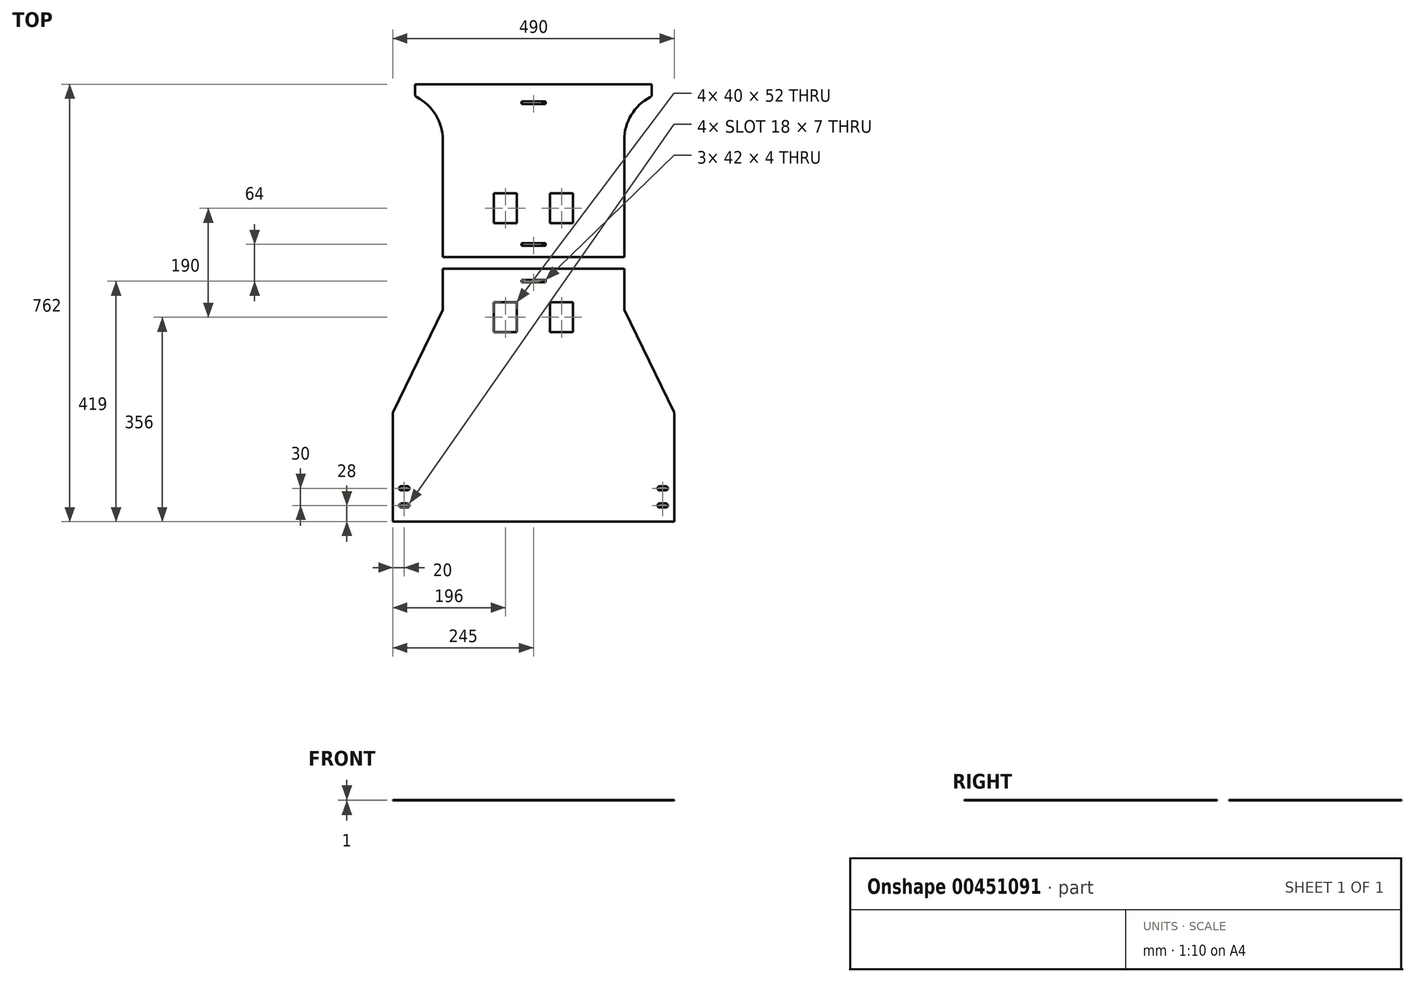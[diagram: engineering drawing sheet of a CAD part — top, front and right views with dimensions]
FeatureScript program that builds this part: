
annotation { "Feature Type Name" : "Feature", "Feature Type Description" : "" }
export const myFeature = defineFeature(function(context is Context, id is Id, definition is map)
    precondition{}
    {
        {
            var Q0;
            Q0=qCreatedBy(makeId("Top.planeOp"),FACE);
            var sketch = newSketch(context, id + "F0", { "sketchPlane" : qUnion([Q0])});
            skLineSegment(sketch, "E0.bottom", {"start": v(0, 0) * mm, "end": v(490, 0) * mm});
            skLineSegment(sketch, "E0.top", {"start": v(0, 190) * mm, "end": v(490, 190) * mm});
            skLineSegment(sketch, "E0.left", {"start": v(0, 0) * mm, "end": v(0, 190) * mm});
            skLineSegment(sketch, "E0.right", {"start": v(490, 0) * mm, "end": v(490, 190) * mm});
            skLineSegment(sketch, "E1", {"start": v(0, 190) * mm, "end": v(87, 369) * mm});
            skLineSegment(sketch, "E2", {"start": v(87, 369) * mm, "end": v(87, 441) * mm});
            skLineSegment(sketch, "E3", {"start": v(87, 441) * mm, "end": v(403, 441) * mm});
            skLineSegment(sketch, "E4", {"start": v(403, 441) * mm, "end": v(403, 369) * mm});
            skLineSegment(sketch, "E5", {"start": v(403, 369) * mm, "end": v(490, 190) * mm});
            skPoint(sketch, "E6", {"position": v(245, 441) * mm});
            skPoint(sketch, "E7", {"position": v(245, 0) * mm});
            skLineSegment(sketch, "E8.bottom", {"start": v(14.5, 24.5) * mm, "end": v(14.5, 31.5) * mm, "construction": true});
            skLineSegment(sketch, "E8.top", {"start": v(25.5, 24.5) * mm, "end": v(25.5, 31.5) * mm, "construction": true});
            skLineSegment(sketch, "E8.left", {"start": v(14.5, 24.5) * mm, "end": v(25.5, 24.5) * mm});
            skLineSegment(sketch, "E8.right", {"start": v(14.5, 31.5) * mm, "end": v(25.5, 31.5) * mm});
            skPoint(sketch, "E8.middle", {"position": v(20, 28) * mm});
            skArc(sketch, "E9", {"start": v(25.5, 24.5) * mm, "mid": v(29, 28) * mm, "end": v(25.5, 31.5) * mm});
            skArc(sketch, "E10", {"start": v(14.5, 31.5) * mm, "mid": v(11, 28) * mm, "end": v(14.5, 24.5) * mm});
            skLineSegment(sketch, "E11.bottom", {"start": v(14.5, 54.5) * mm, "end": v(14.5, 61.5) * mm, "construction": true});
            skLineSegment(sketch, "E11.top", {"start": v(25.5, 54.5) * mm, "end": v(25.5, 61.5) * mm, "construction": true});
            skLineSegment(sketch, "E11.left", {"start": v(14.5, 54.5) * mm, "end": v(25.5, 54.5) * mm});
            skLineSegment(sketch, "E11.right", {"start": v(14.5, 61.5) * mm, "end": v(25.5, 61.5) * mm});
            skPoint(sketch, "E11.middle", {"position": v(20, 58) * mm});
            skArc(sketch, "E12", {"start": v(25.5, 54.5) * mm, "mid": v(29, 58) * mm, "end": v(25.5, 61.5) * mm});
            skArc(sketch, "E13", {"start": v(14.5, 61.5) * mm, "mid": v(11, 58) * mm, "end": v(14.5, 54.5) * mm});
            skLineSegment(sketch, "E14", {"start": v(245, 42.53) * mm, "end": v(245, 125.1) * mm, "construction": true});
            skLineSegment(sketch, "E15.MirrorCS", {"start": v(475.5, 24.5) * mm, "end": v(475.5, 31.5) * mm, "construction": true});
            skArc(sketch, "E16.MirrorCS", {"start": v(464.5, 54.5) * mm, "mid": v(461, 58) * mm, "end": v(464.5, 61.5) * mm});
            skArc(sketch, "E17.MirrorCS", {"start": v(464.5, 24.5) * mm, "mid": v(461, 28) * mm, "end": v(464.5, 31.5) * mm});
            skLineSegment(sketch, "E18.MirrorCS", {"start": v(464.5, 54.5) * mm, "end": v(464.5, 61.5) * mm, "construction": true});
            skArc(sketch, "E19.MirrorCS", {"start": v(475.5, 31.5) * mm, "mid": v(479, 28) * mm, "end": v(475.5, 24.5) * mm});
            skLineSegment(sketch, "E20.MirrorCS", {"start": v(464.5, 24.5) * mm, "end": v(464.5, 31.5) * mm, "construction": true});
            skLineSegment(sketch, "E21.MirrorCS", {"start": v(475.5, 54.5) * mm, "end": v(475.5, 61.5) * mm, "construction": true});
            skArc(sketch, "E22.MirrorCS", {"start": v(475.5, 61.5) * mm, "mid": v(479, 58) * mm, "end": v(475.5, 54.5) * mm});
            skLineSegment(sketch, "E23.MirrorCS", {"start": v(475.5, 31.5) * mm, "end": v(464.5, 31.5) * mm});
            skLineSegment(sketch, "E24.MirrorCS", {"start": v(475.5, 24.5) * mm, "end": v(464.5, 24.5) * mm});
            skLineSegment(sketch, "E25.MirrorCS", {"start": v(475.5, 61.5) * mm, "end": v(464.5, 61.5) * mm});
            skLineSegment(sketch, "E26.MirrorCS", {"start": v(475.5, 54.5) * mm, "end": v(464.5, 54.5) * mm});
            skPoint(sketch, "E27.MirrorP", {"position": v(470, 58) * mm});
            skPoint(sketch, "E28.MirrorP", {"position": v(470, 28) * mm});
            skLineSegment(sketch, "E29", {"start": v(87, 461) * mm, "end": v(403, 461) * mm});
            skLineSegment(sketch, "E30", {"start": v(87, 461) * mm, "end": v(87, 665) * mm});
            skLineSegment(sketch, "E31", {"start": v(87, 665) * mm, "end": v(39, 741) * mm, "construction": true});
            skLineSegment(sketch, "E32", {"start": v(39, 741) * mm, "end": v(39, 762) * mm});
            skLineSegment(sketch, "E33", {"start": v(39, 762) * mm, "end": v(451, 762) * mm});
            skLineSegment(sketch, "E34", {"start": v(451, 762) * mm, "end": v(451, 741) * mm});
            skLineSegment(sketch, "E35", {"start": v(451, 741) * mm, "end": v(403, 665) * mm, "construction": true});
            skLineSegment(sketch, "E36", {"start": v(403, 665) * mm, "end": v(403, 461) * mm});
            skPoint(sketch, "E37", {"position": v(245, 762) * mm});
            skPoint(sketch, "E38", {"position": v(245, 461) * mm});
            skArc(sketch, "E39", {"start": v(87, 665) * mm, "mid": v(74, 709.94) * mm, "end": v(39, 741) * mm});
            skArc(sketch, "E40.MirrorCS", {"start": v(403, 665) * mm, "mid": v(416, 709.94) * mm, "end": v(451, 741) * mm});
            skSolve(sketch);
        }
        {
            var Q0;
            Q0 = qSketchRegion(id + "F0", true);
            extrude(context, id + "F1", {"entities" : qUnion([Q0]), "depth" : 1 * mm, "offsetDistance" : 25 * mm});
        }
        {
            var Q0;
            Q0=makeQuery(id+"F1.opExtrude","SWEPT_EDGE",EDGE,{"disambiguationData":[OSD([sQuery(id+"F0.wireOp",EDGE,"E32"),sQuery(id+"F0.wireOp",EDGE,"E39")])]});
            var Q1;
            Q1=makeQuery(id+"F1.opExtrude","SWEPT_EDGE",EDGE,{"disambiguationData":[OSD([sQuery(id+"F0.wireOp",EDGE,"E34"),sQuery(id+"F0.wireOp",EDGE,"E40.MirrorCS")])]});
            var Q2;
            Q2=makeQuery(id+"F1.opExtrude","SWEPT_EDGE",EDGE,{"disambiguationData":[OSD([sQuery(id+"F0.wireOp",EDGE,"E0.top"),sQuery(id+"F0.wireOp",EDGE,"E0.left"),sQuery(id+"F0.wireOp",EDGE,"E1")])]});
            var Q3;
            Q3=makeQuery(id+"F1.opExtrude","SWEPT_EDGE",EDGE,{"disambiguationData":[OSD([sQuery(id+"F0.wireOp",EDGE,"E0.top"),sQuery(id+"F0.wireOp",EDGE,"E0.right"),sQuery(id+"F0.wireOp",EDGE,"E5")])]});
            fillet(context, id + "F2", {"entities" : qUnion([Q0, Q1, Q2, Q3]), "tangentPropagation" : true, "radius" : 5 * mm, "defaultsChanged" : false, "vertexSettings" : [], "allowEdgeOverflow" : false});
        }
        {
            var Q0;
            Q0=makeQuery(id+"F1.opExtrude","CAP_FACE",FACE,{"disambiguationData":[OSD([sQuery(id+"F0.wireOp",EDGE,"E0.bottom"),sQuery(id+"F0.wireOp",EDGE,"E0.left"),sQuery(id+"F0.wireOp",EDGE,"E0.right"),sQuery(id+"F0.wireOp",EDGE,"E1"),sQuery(id+"F0.wireOp",EDGE,"E2"),sQuery(id+"F0.wireOp",EDGE,"E3"),sQuery(id+"F0.wireOp",EDGE,"E4"),sQuery(id+"F0.wireOp",EDGE,"E5"),sQuery(id+"F0.wireOp",EDGE,"E8.left"),sQuery(id+"F0.wireOp",EDGE,"E8.right"),sQuery(id+"F0.wireOp",EDGE,"E9"),sQuery(id+"F0.wireOp",EDGE,"E10"),sQuery(id+"F0.wireOp",EDGE,"E11.left"),sQuery(id+"F0.wireOp",EDGE,"E11.right"),sQuery(id+"F0.wireOp",EDGE,"E12"),sQuery(id+"F0.wireOp",EDGE,"E13"),sQuery(id+"F0.wireOp",EDGE,"E16.MirrorCS"),sQuery(id+"F0.wireOp",EDGE,"E17.MirrorCS"),sQuery(id+"F0.wireOp",EDGE,"E19.MirrorCS"),sQuery(id+"F0.wireOp",EDGE,"E22.MirrorCS"),sQuery(id+"F0.wireOp",EDGE,"E23.MirrorCS"),sQuery(id+"F0.wireOp",EDGE,"E24.MirrorCS"),sQuery(id+"F0.wireOp",EDGE,"E25.MirrorCS"),sQuery(id+"F0.wireOp",EDGE,"E26.MirrorCS")])],"isStart":false});
            var sketch = newSketch(context, id + "F3", { "sketchPlane" : qUnion([Q0])});
            skPoint(sketch, "E41.middle.positionSnap0", {"position": v(245, 0) * mm});
            skPoint(sketch, "E41.centerSnap0", {"position": v(245, 0) * mm});
            skLineSegment(sketch, "E42.bottom", {"start": v(211, 330) * mm, "end": v(216, 330) * mm});
            skLineSegment(sketch, "E42.top", {"start": v(211, 377) * mm, "end": v(216, 377) * mm});
            skLineSegment(sketch, "E42.left", {"start": v(211, 330) * mm, "end": v(211, 377) * mm, "construction": true});
            skLineSegment(sketch, "E42.right", {"start": v(216, 330) * mm, "end": v(216, 377) * mm});
            skLineSegment(sketch, "E43.bottom", {"start": v(216, 377) * mm, "end": v(176, 377) * mm, "construction": true});
            skLineSegment(sketch, "E43.top", {"start": v(216, 382) * mm, "end": v(176, 382) * mm});
            skLineSegment(sketch, "E43.left", {"start": v(216, 377) * mm, "end": v(216, 382) * mm});
            skLineSegment(sketch, "E43.right", {"start": v(176, 377) * mm, "end": v(176, 382) * mm});
            skLineSegment(sketch, "E44", {"start": v(245, 0) * mm, "end": v(245, -104.71) * mm, "construction": true});
            skLineSegment(sketch, "E45.bottom", {"start": v(266, 417) * mm, "end": v(224, 417) * mm});
            skLineSegment(sketch, "E45.top", {"start": v(266, 421) * mm, "end": v(224, 421) * mm});
            skLineSegment(sketch, "E45.left", {"start": v(266, 417) * mm, "end": v(266, 421) * mm});
            skLineSegment(sketch, "E45.right", {"start": v(224, 417) * mm, "end": v(224, 421) * mm});
            skPoint(sketch, "E45.middle", {"position": v(245, 419) * mm});
            skPoint(sketch, "E45.middle.positionSnap0", {"position": v(245, 441) * mm});
            skPoint(sketch, "E45.centerSnap0", {"position": v(245, 441) * mm});
            skLineSegment(sketch, "E46", {"start": v(176, 377) * mm, "end": v(176, 330) * mm});
            skLineSegment(sketch, "E47", {"start": v(176, 330) * mm, "end": v(211, 330) * mm});
            skLineSegment(sketch, "E48.MirrorCS", {"start": v(279, 377) * mm, "end": v(274, 377) * mm});
            skLineSegment(sketch, "E49.MirrorCS", {"start": v(314, 330) * mm, "end": v(279, 330) * mm});
            skLineSegment(sketch, "E50.MirrorCS", {"start": v(279, 330) * mm, "end": v(279, 377) * mm, "construction": true});
            skLineSegment(sketch, "E51.MirrorCS", {"start": v(274, 377) * mm, "end": v(314, 377) * mm, "construction": true});
            skLineSegment(sketch, "E52.MirrorCS", {"start": v(274, 330) * mm, "end": v(274, 377) * mm});
            skLineSegment(sketch, "E53.MirrorCS", {"start": v(279, 330) * mm, "end": v(274, 330) * mm});
            skLineSegment(sketch, "E54.MirrorCS", {"start": v(314, 377) * mm, "end": v(314, 330) * mm});
            skLineSegment(sketch, "E55.MirrorCS", {"start": v(274, 377) * mm, "end": v(274, 382) * mm});
            skLineSegment(sketch, "E56.MirrorCS", {"start": v(274, 382) * mm, "end": v(314, 382) * mm});
            skLineSegment(sketch, "E57.MirrorCS", {"start": v(314, 377) * mm, "end": v(314, 382) * mm});
            skSolve(sketch);
        }
        {
            var Q0;
            Q0 = qSketchRegion(id + "F3", true);
            extrude(context, id + "F4", {"entities" : qUnion([Q0]), "operationType" : NewBodyOperationType.REMOVE, "oppositeDirection" : true, "depth" : 25 * mm, "offsetDistance" : 25 * mm});
        }
        {
            var Q0;
            Q0=makeQuery(id+"F1.opExtrude","CAP_FACE",FACE,{"disambiguationData":[OSD([sQuery(id+"F0.wireOp",EDGE,"E29"),sQuery(id+"F0.wireOp",EDGE,"E30"),sQuery(id+"F0.wireOp",EDGE,"E32"),sQuery(id+"F0.wireOp",EDGE,"E33"),sQuery(id+"F0.wireOp",EDGE,"E34"),sQuery(id+"F0.wireOp",EDGE,"E36"),sQuery(id+"F0.wireOp",EDGE,"E39"),sQuery(id+"F0.wireOp",EDGE,"E40.MirrorCS")])],"isStart":false});
            var sketch = newSketch(context, id + "F5", { "sketchPlane" : qUnion([Q0])});
            skLineSegment(sketch, "E58.bottom", {"start": v(266, 481) * mm, "end": v(224, 481) * mm});
            skLineSegment(sketch, "E58.top", {"start": v(266, 485) * mm, "end": v(224, 485) * mm});
            skLineSegment(sketch, "E58.left", {"start": v(266, 481) * mm, "end": v(266, 485) * mm});
            skLineSegment(sketch, "E58.right", {"start": v(224, 481) * mm, "end": v(224, 485) * mm});
            skPoint(sketch, "E58.middle", {"position": v(245, 483) * mm});
            skPoint(sketch, "E58.middle.positionSnap0", {"position": v(245, 762) * mm});
            skPoint(sketch, "E58.centerSnap0", {"position": v(245, 762) * mm});
            skLineSegment(sketch, "E59.bottom", {"start": v(211, 572) * mm, "end": v(216, 572) * mm});
            skLineSegment(sketch, "E59.top", {"start": v(211, 525) * mm, "end": v(216, 525) * mm});
            skLineSegment(sketch, "E59.left", {"start": v(211, 572) * mm, "end": v(211, 525) * mm, "construction": true});
            skLineSegment(sketch, "E59.right", {"start": v(216, 572) * mm, "end": v(216, 525) * mm});
            skLineSegment(sketch, "E60.bottom", {"start": v(216, 525) * mm, "end": v(176, 525) * mm, "construction": true});
            skLineSegment(sketch, "E60.top", {"start": v(216, 520) * mm, "end": v(176, 520) * mm});
            skLineSegment(sketch, "E60.left", {"start": v(216, 525) * mm, "end": v(216, 520) * mm});
            skLineSegment(sketch, "E60.right", {"start": v(176, 525) * mm, "end": v(176, 520) * mm});
            skLineSegment(sketch, "E61", {"start": v(211, 572) * mm, "end": v(176, 572) * mm});
            skLineSegment(sketch, "E62", {"start": v(176, 572) * mm, "end": v(176, 525) * mm});
            skLineSegment(sketch, "E63", {"start": v(245, 762) * mm, "end": v(245, 730.96) * mm, "construction": true});
            skLineSegment(sketch, "E64.MirrorCS", {"start": v(279, 525) * mm, "end": v(274, 525) * mm});
            skLineSegment(sketch, "E65.MirrorCS", {"start": v(279, 572) * mm, "end": v(274, 572) * mm});
            skLineSegment(sketch, "E66.MirrorCS", {"start": v(274, 525) * mm, "end": v(274, 520) * mm});
            skLineSegment(sketch, "E67.MirrorCS", {"start": v(314, 525) * mm, "end": v(314, 520) * mm});
            skLineSegment(sketch, "E68.MirrorCS", {"start": v(279, 572) * mm, "end": v(314, 572) * mm});
            skLineSegment(sketch, "E69.MirrorCS", {"start": v(314, 572) * mm, "end": v(314, 525) * mm});
            skLineSegment(sketch, "E70.MirrorCS", {"start": v(274, 572) * mm, "end": v(274, 525) * mm});
            skLineSegment(sketch, "E71.MirrorCS", {"start": v(279, 572) * mm, "end": v(279, 525) * mm, "construction": true});
            skLineSegment(sketch, "E72.MirrorCS", {"start": v(274, 525) * mm, "end": v(314, 525) * mm, "construction": true});
            skLineSegment(sketch, "E73.MirrorCS", {"start": v(274, 520) * mm, "end": v(314, 520) * mm});
            skLineSegment(sketch, "E74.bottom", {"start": v(266, 728) * mm, "end": v(224, 728) * mm});
            skLineSegment(sketch, "E74.top", {"start": v(266, 732) * mm, "end": v(224, 732) * mm});
            skLineSegment(sketch, "E74.left", {"start": v(266, 728) * mm, "end": v(266, 732) * mm});
            skLineSegment(sketch, "E74.right", {"start": v(224, 728) * mm, "end": v(224, 732) * mm});
            skPoint(sketch, "E74.middle", {"position": v(245, 730) * mm});
            skSolve(sketch);
        }
        {
            var Q0;
            Q0 = qSketchRegion(id + "F5", true);
            extrude(context, id + "F6", {"entities" : qUnion([Q0]), "operationType" : NewBodyOperationType.REMOVE, "oppositeDirection" : true, "depth" : 25 * mm, "offsetDistance" : 25 * mm});
        }
    });
